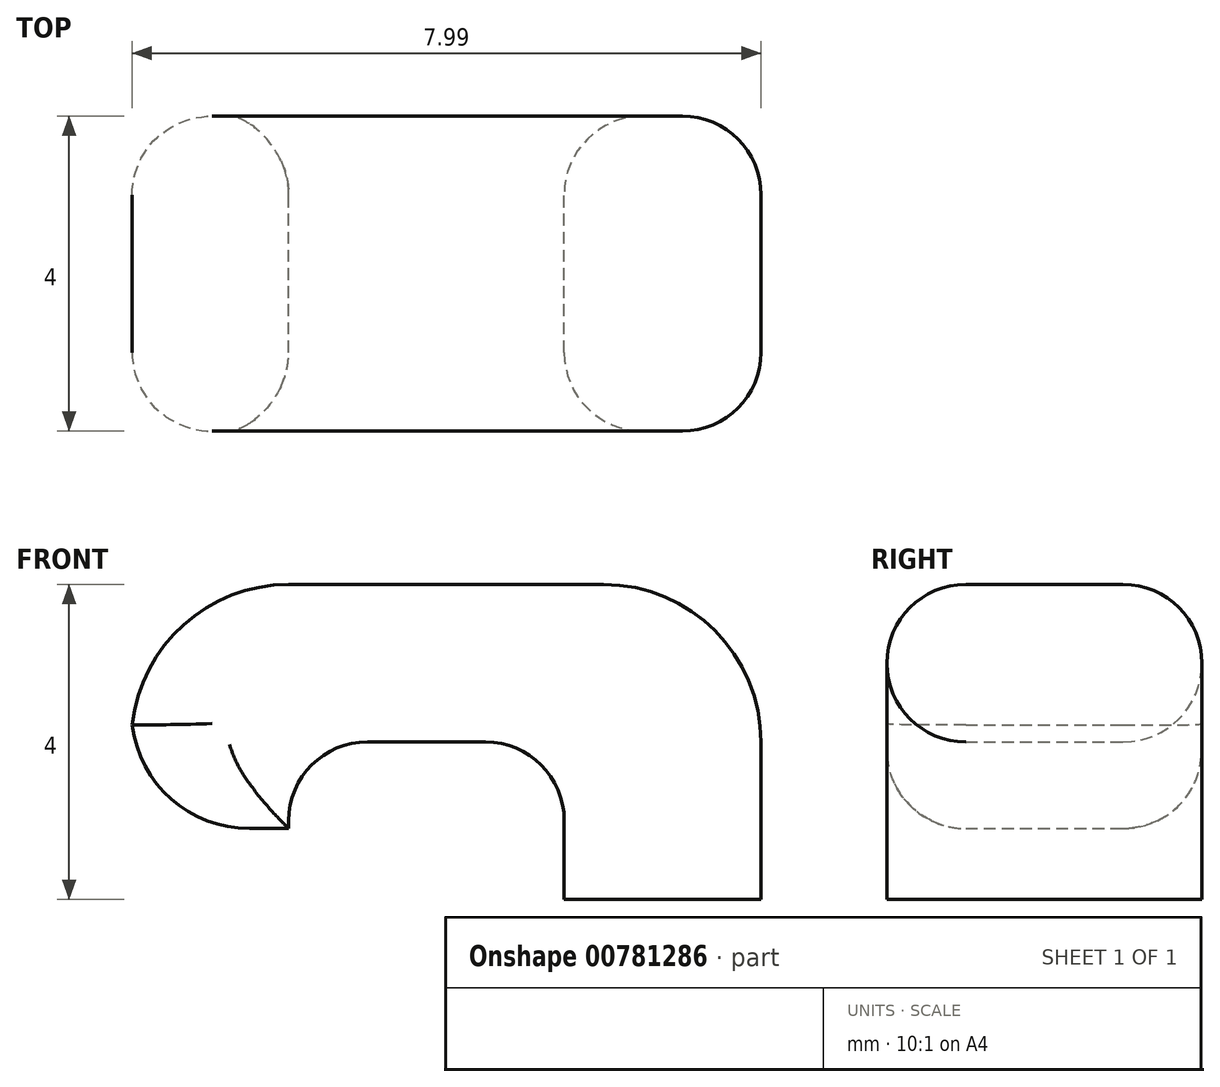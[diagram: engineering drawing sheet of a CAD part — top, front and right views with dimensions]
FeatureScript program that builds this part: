
annotation { "Feature Type Name" : "Feature", "Feature Type Description" : "" }
export const myFeature = defineFeature(function(context is Context, id is Id, definition is map)
    precondition{}
    {
        {
            var Q0;
            Q0=qCreatedBy(makeId("Front.planeOp"),FACE);
            var sketch = newSketch(context, id + "F0", { "sketchPlane" : qUnion([Q0])});
            skPoint(sketch, "E0.middle", {"position": v(0, 0) * mm});
            skLineSegment(sketch, "E1", {"start": v(-2.5, 4) * mm, "end": v(-6, 4) * mm});
            skLineSegment(sketch, "E2", {"start": v(-8, 2.4) * mm, "end": v(-8, 2) * mm});
            skLineSegment(sketch, "E3", {"start": v(-6.5, 0.9) * mm, "end": v(-6, 0.9) * mm});
            skLineSegment(sketch, "E4", {"start": v(-6, 0.9) * mm, "end": v(-6, 1) * mm});
            skLineSegment(sketch, "E5", {"start": v(-5, 2) * mm, "end": v(-3.5, 2) * mm});
            skLineSegment(sketch, "E6", {"start": v(-2.5, 4) * mm, "end": v(-2, 4) * mm});
            skLineSegment(sketch, "E7", {"start": v(0, 2) * mm, "end": v(0, 0) * mm});
            skLineSegment(sketch, "E8", {"start": v(-2.5, 0) * mm, "end": v(-2.5, 1) * mm});
            skLineSegment(sketch, "E9", {"start": v(-2.5, 0) * mm, "end": v(0, 0) * mm});
            skLineSegment(sketch, "E10", {"start": v(-2.5, 2) * mm, "end": v(-2.5, 4) * mm, "construction": true});
            skPoint(sketch, "E11.visualSharp", {"position": v(-8, 0.9) * mm});
            skArc(sketch, "E11.filletArc", {"start": v(-8, 2.4) * mm, "mid": v(-7.56, 1.34) * mm, "end": v(-6.5, 0.9) * mm});
            skPoint(sketch, "E12.visualSharp", {"position": v(-8, 4) * mm});
            skArc(sketch, "E12.filletArc", {"start": v(-6, 4) * mm, "mid": v(-7.41, 3.41) * mm, "end": v(-8, 2) * mm});
            skArc(sketch, "E13.filletArc", {"start": v(-5, 2) * mm, "mid": v(-5.7, 1.7) * mm, "end": v(-6, 1) * mm});
            skPoint(sketch, "E14.visualSharp", {"position": v(-2.5, 2) * mm});
            skArc(sketch, "E14.filletArc", {"start": v(-2.5, 1) * mm, "mid": v(-2.8, 1.7) * mm, "end": v(-3.5, 2) * mm});
            skPoint(sketch, "E15.visualSharp", {"position": v(0, 4) * mm});
            skArc(sketch, "E15.filletArc", {"start": v(0, 2) * mm, "mid": v(-0.59, 3.41) * mm, "end": v(-2, 4) * mm});
            skSolve(sketch);
        }
        {
            var Q0;
            Q0=makeQuery(id+"F0.imprint","IMPRINT",FACE,{"disambiguationData":[TD([[makeQuery(id+"F0.imprint","IMPRINT",EDGE,{"derivedFrom":sQuery(id+"F0.wireOp",EDGE,"E1")}),1.0]])]});
            extrude(context, id + "F1", {"entities" : qUnion([Q0]), "endBound" : BoundingType.SYMMETRIC, "depth" : 4 * mm, "offsetDistance" : 25 * mm});
        }
        {
            var Q0;
            Q0=makeQuery(id+"F1.opExtrude","CAP_EDGE",EDGE,{"disambiguationData":[OSD([sQuery(id+"F0.wireOp",EDGE,"E8")])],"isStart":false});
            var Q1;
            Q1=makeQuery(id+"F1.opExtrude","CAP_EDGE",EDGE,{"disambiguationData":[OSD([sQuery(id+"F0.wireOp",EDGE,"E7")])],"isStart":false});
            var Q2;
            Q2=makeQuery(id+"F1.opExtrude","CAP_EDGE",EDGE,{"disambiguationData":[OSD([sQuery(id+"F0.wireOp",EDGE,"E8")])],"isStart":true});
            var Q3;
            Q3=makeQuery(id+"F1.opExtrude","CAP_EDGE",EDGE,{"disambiguationData":[OSD([sQuery(id+"F0.wireOp",EDGE,"E7")])],"isStart":true});
            var Q4;
            Q4=makeQuery(id+"F1.opExtrude","CAP_EDGE",EDGE,{"disambiguationData":[OSD([sQuery(id+"F0.wireOp",EDGE,"E14.filletArc")])],"isStart":false});
            var Q5;
            Q5=makeQuery(id+"F1.opExtrude","CAP_EDGE",EDGE,{"disambiguationData":[OSD([sQuery(id+"F0.wireOp",EDGE,"E5")])],"isStart":false});
            var Q6;
            Q6=makeQuery(id+"F1.opExtrude","CAP_EDGE",EDGE,{"disambiguationData":[OSD([sQuery(id+"F0.wireOp",EDGE,"E13.filletArc")])],"isStart":false});
            var Q7;
            Q7=makeQuery(id+"F1.opExtrude","CAP_EDGE",EDGE,{"disambiguationData":[OSD([sQuery(id+"F0.wireOp",EDGE,"E4")])],"isStart":false});
            var Q8;
            Q8=makeQuery(id+"F1.opExtrude","CAP_EDGE",EDGE,{"disambiguationData":[OSD([sQuery(id+"F0.wireOp",EDGE,"E11.filletArc")])],"isStart":false});
            var Q9;
            Q9=makeQuery(id+"F1.opExtrude","CAP_EDGE",EDGE,{"disambiguationData":[OSD([sQuery(id+"F0.wireOp",EDGE,"E3")])],"isStart":false});
            var Q10;
            Q10=makeQuery(id+"F1.opExtrude","CAP_EDGE",EDGE,{"disambiguationData":[OSD([sQuery(id+"F0.wireOp",EDGE,"E12.filletArc")])],"isStart":false});
            var Q11;
            Q11=makeQuery(id+"F1.opExtrude","CAP_EDGE",EDGE,{"disambiguationData":[OSD([sQuery(id+"F0.wireOp",EDGE,"E1"),sQuery(id+"F0.wireOp",EDGE,"E6")])],"isStart":false});
            var Q12;
            Q12=makeQuery(id+"F1.opExtrude","CAP_EDGE",EDGE,{"disambiguationData":[OSD([sQuery(id+"F0.wireOp",EDGE,"E15.filletArc")])],"isStart":false});
            var Q13;
            Q13=makeQuery(id+"F1.opExtrude","CAP_EDGE",EDGE,{"disambiguationData":[OSD([sQuery(id+"F0.wireOp",EDGE,"E15.filletArc")])],"isStart":true});
            var Q14;
            Q14=makeQuery(id+"F1.opExtrude","CAP_EDGE",EDGE,{"disambiguationData":[OSD([sQuery(id+"F0.wireOp",EDGE,"E1"),sQuery(id+"F0.wireOp",EDGE,"E6")])],"isStart":true});
            var Q15;
            Q15=makeQuery(id+"F1.opExtrude","CAP_EDGE",EDGE,{"disambiguationData":[OSD([sQuery(id+"F0.wireOp",EDGE,"E12.filletArc")])],"isStart":true});
            var Q16;
            Q16=makeQuery(id+"F1.opExtrude","CAP_EDGE",EDGE,{"disambiguationData":[OSD([sQuery(id+"F0.wireOp",EDGE,"E11.filletArc")])],"isStart":true});
            var Q17;
            Q17=makeQuery(id+"F1.opExtrude","CAP_EDGE",EDGE,{"disambiguationData":[OSD([sQuery(id+"F0.wireOp",EDGE,"E3")])],"isStart":true});
            var Q18;
            Q18=makeQuery(id+"F1.opExtrude","CAP_EDGE",EDGE,{"disambiguationData":[OSD([sQuery(id+"F0.wireOp",EDGE,"E4")])],"isStart":true});
            var Q19;
            Q19=makeQuery(id+"F1.opExtrude","CAP_EDGE",EDGE,{"disambiguationData":[OSD([sQuery(id+"F0.wireOp",EDGE,"E13.filletArc")])],"isStart":true});
            var Q20;
            Q20=makeQuery(id+"F1.opExtrude","CAP_EDGE",EDGE,{"disambiguationData":[OSD([sQuery(id+"F0.wireOp",EDGE,"E5")])],"isStart":true});
            var Q21;
            Q21=makeQuery(id+"F1.opExtrude","CAP_EDGE",EDGE,{"disambiguationData":[OSD([sQuery(id+"F0.wireOp",EDGE,"E14.filletArc")])],"isStart":true});
            fillet(context, id + "F2", {"entities" : qUnion([Q0, Q1, Q2, Q3, Q4, Q5, Q6, Q7, Q8, Q9, Q10, Q11, Q12, Q13, Q14, Q15, Q16, Q17, Q18, Q19, Q20, Q21]), "radius" : 1 * mm, "tangentPropagation" : true, "allowEdgeOverflow" : false});
        }
    });
